# Revit family: K Series Bar Joist-Rod Web-Extended Ends
name_source: partatom
category: Structural Framing
revit_build: Autodesk Revit Structure 2012 (Build: 20110916_2132(x64)
units: mm (PartAtom-declared; Revit-internal decimal feet)

## types (23) — shared parameters
Assembly Code = B1010350
Chord Thickness = 0' - 0 1/4"
Cord Leg = 0' - 1 1/4"
Description = Steel Joist
Rendering Material = <By Category>
Seat Length = 0' - 4"
Web Thickness = 0' - 0 3/8"

## per-type parameters (varying)
| type | Depth | End Panel | Pounds Per Foot | Wt |
| 10K1 | 0' - 10" | 1' - 8" | 5 | 5 |
| K JOIST | 0' - 10" | 1' - 8" | 5 | 5 |
| 26K7 | 2' - 2" | 4' - 4" | 11 | 11 |
| 24K7 | 2' - 0" | 4' - 0" | 10 | 10 |
| 24K4 | 2' - 0" | 4' - 0" | 8 | 8 |
| 22K9 | 1' - 10" | 3' - 8" | 11 | 11 |
| 22K7 | 1' - 10" | 3' - 8" | 10 | 10 |
| 22K6 | 1' - 10" | 3' - 8" | 9 | 9 |
| 22K5 | 1' - 10" | 3' - 8" | 9 | 9 |
| 18K5 | 1' - 6" | 3' - 0" | 8 | 8 |
| 28K9 | 2' - 4" | 4' - 8" | 13 | 13 |
| 20K3 | 1' - 8" | 3' - 4" | 7 | 7 |
| 18K3 | 1' - 6" | 3' - 0" | 7 | 7 |
| 16K7 | 1' - 4" | 2' - 8" | 9 | 9 |
| 16K6 | 1' - 4" | 2' - 8" | 8 | 8 |
| 16K5 | 1' - 4" | 2' - 8" | 8 | 8 |
| K-SERIES JOISTS | 1' - 4" | 2' - 8" | 6 | 6 |
| 22K4 | 1' - 10" | 3' - 8" | 8 | 8 |
| 20K4 | 1' - 8" | 3' - 4" | 8 | 8 |
| 18K4 | 1' - 6" | 3' - 0" | 7 | 7 |
| 16K2 | 1' - 4" | 2' - 8" | 6 | 6 |
| 14K1 | 1' - 2" | 2' - 4" | 5 | 5 |
| 12K1 | 1' - 0" | 2' - 0" | 5 | 5 |

## geometry (parser evidence)
native form markers: Sweep x5
no freeform markers — native parametric forms only
